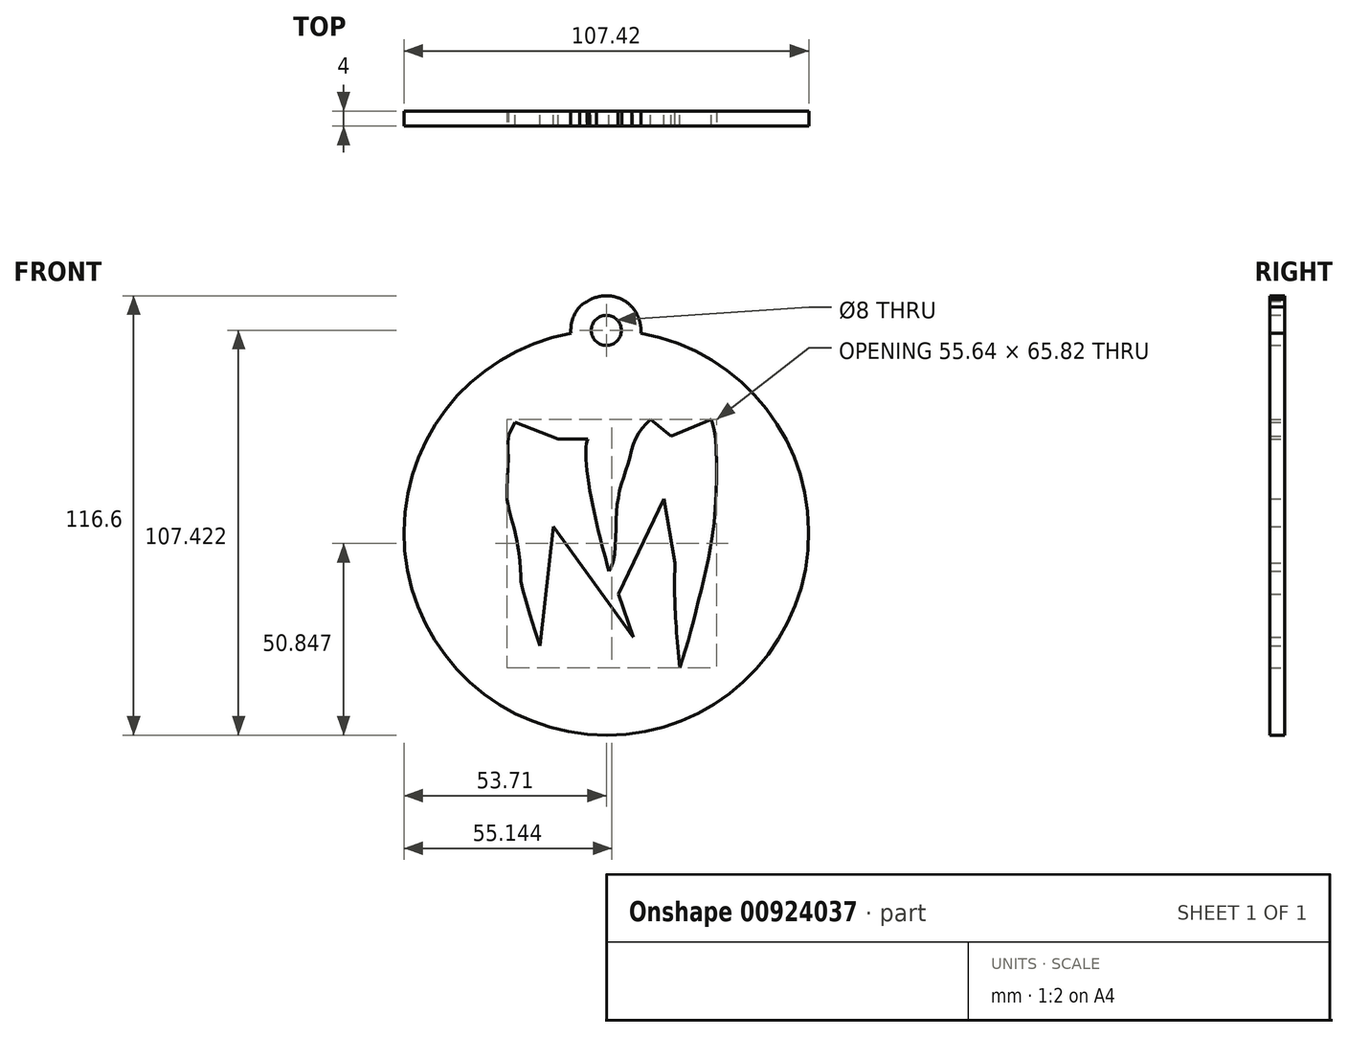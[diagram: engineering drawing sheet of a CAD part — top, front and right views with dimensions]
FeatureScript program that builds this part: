
annotation { "Feature Type Name" : "Feature", "Feature Type Description" : "" }
export const myFeature = defineFeature(function(context is Context, id is Id, definition is map)
    precondition{}
    {
        {
            var Q0;
            Q0=qCreatedBy(makeId("Front.planeOp"),FACE);
            var sketch = newSketch(context, id + "F0", { "sketchPlane" : qUnion([Q0])});
            skCircle(sketch, "E0", {"center": v(0, 0) * mm, "radius": 53.71 * mm});
            skArc(sketch, "E1", {"start": v(0, 62.9) * mm, "mid": v(6.76, 59.92) * mm, "end": v(9.15, 52.93) * mm});
            skArc(sketch, "E2", {"start": v(-5.42, 61.4) * mm, "mid": v(-8.54, 57.67) * mm, "end": v(-9.38, 52.89) * mm});
            skArc(sketch, "E3", {"start": v(0, 62.9) * mm, "mid": v(-2.61, 62.51) * mm, "end": v(-5, 61.4) * mm});
            skPoint(sketch, "E4.8.internal.snap0", {"position": v(6.76, 59.92) * mm});
            skFitSpline(sketch, "E4", {"points": [v(9.15, 52.93) * mm, v(9.15, 54.5) * mm, v(8.64, 56.82) * mm, v(6.76, 59.92) * mm, v(4.15, 61.9) * mm, v(3.06, 62.36) * mm, v(-2.61, 62.51) * mm, v(-5, 61.4) * mm, v(-7.08, 59.92) * mm, v(-9.38, 52.89) * mm], "startDerivative": vector(0.6, 19.1) * mm, "endDerivative": vector(-10.89, -49.75) * mm});
            skFitSpline(sketch, "E5", {"points": [v(19.51, -35.77) * mm, v(22.64, -25.37) * mm, v(25.76, -12.62) * mm, v(28.62, 3) * mm, v(28.88, 25.62) * mm, v(27.84, 30.05) * mm], "startDerivative": vector(17.21, 54.48) * mm, "endDerivative": vector(-9.79, 28.04) * mm});
            skLineSegment(sketch, "E6", {"start": v(27.84, 30.05) * mm, "end": v(17.17, 25.62) * mm});
            skLineSegment(sketch, "E7", {"start": v(17.17, 25.62) * mm, "end": v(11.7, 30.05) * mm});
            skFitSpline(sketch, "E8", {"points": [v(11.7, 30.05) * mm, v(8.07, 25.62) * mm, v(5.99, 19.12) * mm, v(3.64, 11.58) * mm, v(2.6, 3.25) * mm, v(1.82, -7.68) * mm, v(0, -11.06) * mm], "startDerivative": vector(-27.44, -27.13) * mm, "endDerivative": vector(-17.11, -22.08) * mm});
            skFitSpline(sketch, "E9", {"points": [v(0.7, -10.15) * mm, v(-3.64, 7.41) * mm, v(-5.46, 21.72) * mm, v(-4.94, 24.84) * mm], "startDerivative": vector(-10.81, 39.69) * mm, "endDerivative": vector(3.97, 13.97) * mm});
            skLineSegment(sketch, "E10", {"start": v(-4.94, 24.84) * mm, "end": v(-12.75, 24.84) * mm});
            skLineSegment(sketch, "E11", {"start": v(-12.75, 24.84) * mm, "end": v(-24.2, 29.27) * mm});
            skFitSpline(sketch, "E12", {"points": [v(-24.2, 29.27) * mm, v(-25.98, 25.28) * mm, v(-25.98, 19.2) * mm, v(-26.34, 9.18) * mm, v(-24.2, 0) * mm, v(-22.76, -9.78) * mm, v(-22.58, -13.18) * mm, v(-17.57, -30) * mm], "startDerivative": vector(-21.68, -36.26) * mm, "endDerivative": vector(32.07, -97.63) * mm});
            skLineSegment(sketch, "E13", {"start": v(-17.57, -30) * mm, "end": v(-14, 1.67) * mm});
            skLineSegment(sketch, "E14", {"start": v(-14, 1.67) * mm, "end": v(7.11, -27.67) * mm});
            skLineSegment(sketch, "E15", {"start": v(7.11, -27.67) * mm, "end": v(3.18, -16.22) * mm});
            skLineSegment(sketch, "E16", {"start": v(3.18, -16.22) * mm, "end": v(15.34, 9) * mm});
            skLineSegment(sketch, "E17", {"start": v(15.34, 9) * mm, "end": v(18.2, -8) * mm});
            skFitSpline(sketch, "E18", {"points": [v(18.2, -8) * mm, v(18.2, -19.44) * mm, v(19.51, -35.77) * mm], "startDerivative": vector(-0.55, -24.04) * mm, "endDerivative": vector(3.06, -31.3) * mm});
            skSolve(sketch);
        }
        {
            var Q0;
            Q0 = qSketchRegion(id + "F0", true);
            extrude(context, id + "F1", {"entities" : qUnion([Q0]), "depth" : 4 * mm, "offsetDistance" : 25.4 * mm});
        }
        {
            var Q0;
            Q0=sQuery(id+"F0.wireOp",VERTEX,"E1.center");
            var Q1;
            Q1=makeQuery(id+"F1.opExtrude","SWEPT_BODY",BODY,{"disambiguationData":[OSD([sQuery(id+"F0.wireOp",EDGE,"E0"),sQuery(id+"F0.wireOp",EDGE,"E1"),sQuery(id+"F0.wireOp",EDGE,"E2"),sQuery(id+"F0.wireOp",EDGE,"E3"),sQuery(id+"F0.wireOp",EDGE,"E4")])]});
            hole(context, id + "F2", {"style" : HoleStyle.SIMPLE, "endStyle" : HoleEndStyle.THROUGH, "oppositeDirection" : true, "holeDiameter" : 8 * mm, "majorDiameter" : 5 * mm, "isTappedThrough" : true, "tappedDepth" : 12 * mm, "tapClearance" : 3, "locations" : qUnion([Q0]), "scope" : qUnion([Q1])});
        }
    });
